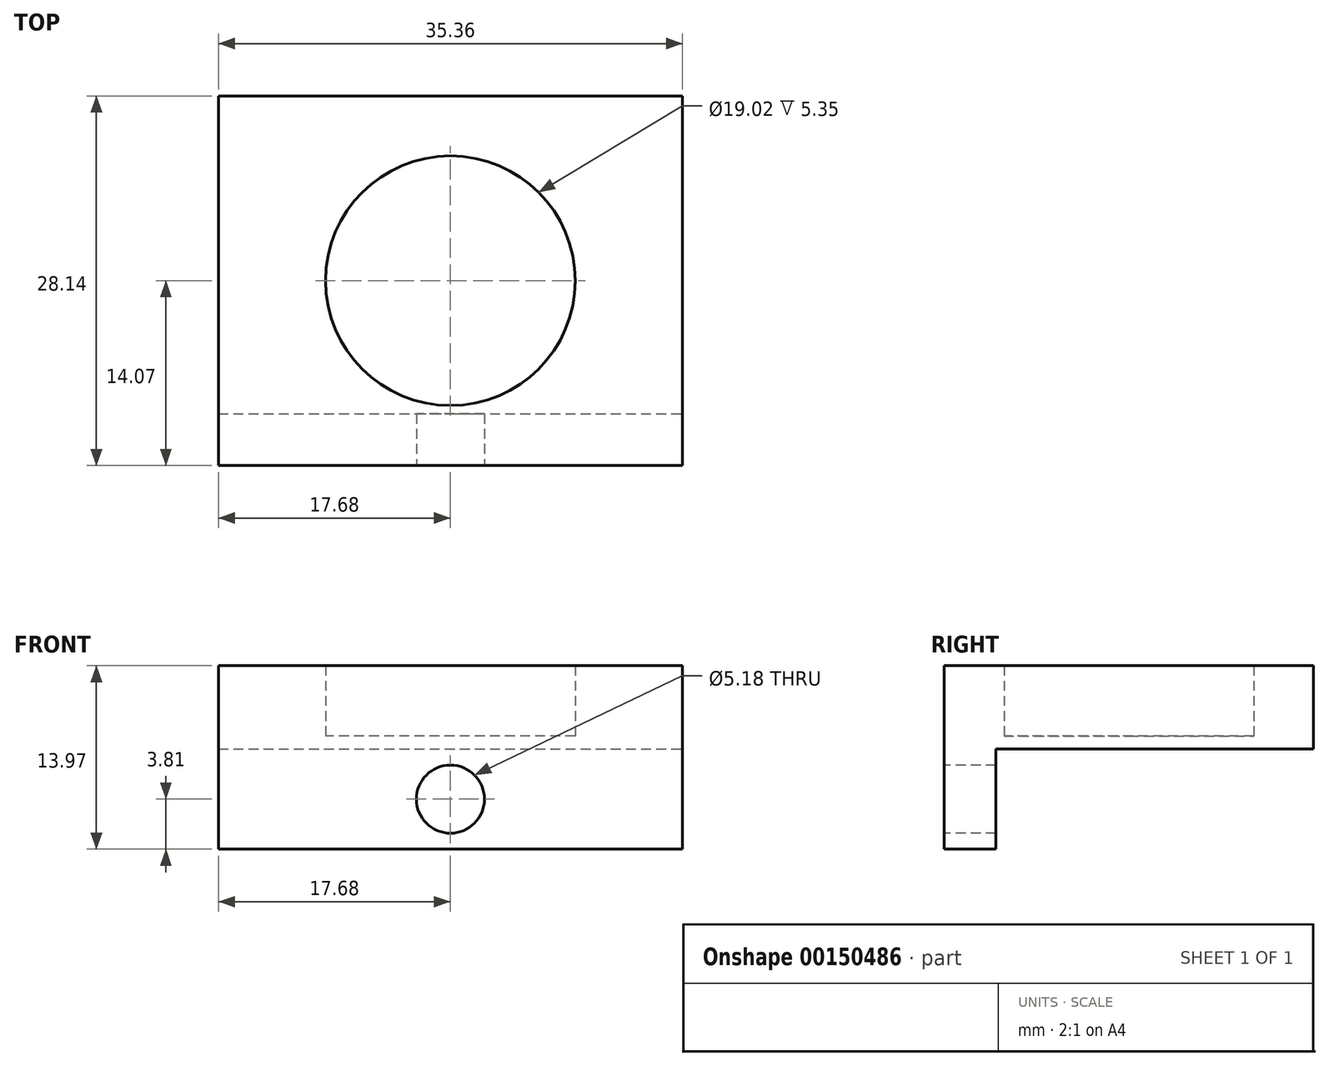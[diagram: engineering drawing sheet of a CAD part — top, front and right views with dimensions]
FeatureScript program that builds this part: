
annotation { "Feature Type Name" : "Feature", "Feature Type Description" : "" }
export const myFeature = defineFeature(function(context is Context, id is Id, definition is map)
    precondition{}
    {
        {
            var Q0;
            Q0=qCreatedBy(makeId("Top.planeOp"),FACE);
            var sketch = newSketch(context, id + "F0", { "sketchPlane" : qUnion([Q0])});
            skLineSegment(sketch, "E0.bottom", {"start": v(-17.68, 14.07) * mm, "end": v(17.68, 14.07) * mm});
            skLineSegment(sketch, "E0.top", {"start": v(-17.68, -14.07) * mm, "end": v(17.68, -14.07) * mm});
            skLineSegment(sketch, "E0.left", {"start": v(-17.68, 14.07) * mm, "end": v(-17.68, -14.07) * mm});
            skLineSegment(sketch, "E0.right", {"start": v(17.68, 14.07) * mm, "end": v(17.68, -14.07) * mm});
            skPoint(sketch, "E0.middle", {"position": v(0, 0) * mm});
            skCircle(sketch, "E1", {"center": v(0, 0) * mm, "radius": 9.5 * mm});
            skSolve(sketch);
        }
        {
            var Q0;
            Q0=makeQuery(id+"F0.imprint","IMPRINT",FACE,{"disambiguationData":[TD([[makeQuery(id+"F0.imprint","IMPRINT",EDGE,{"derivedFrom":sQuery(id+"F0.wireOp",EDGE,"E0.bottom")}),-1.0]])]});
            var Q1;
            Q1=makeQuery(id+"F0.imprint","IMPRINT",FACE,{"disambiguationData":[TD([[makeQuery(id+"F0.imprint","IMPRINT",EDGE,{"derivedFrom":sQuery(id+"F0.wireOp",EDGE,"E1")}),1.0]])]});
            extrude(context, id + "F1", {"entities" : qUnion([Q0, Q1]), "depth" : 1 * mm});
        }
        {
            var Q0;
            Q0 = qSketchRegion(id + "F0", true);
            extrude(context, id + "F2", {"entities" : qUnion([Q0]), "operationType" : NewBodyOperationType.ADD, "depth" : 6.35 * mm});
        }
        {
            var Q0;
            {var subQ0=sQuery(id+"F0.wireOp",EDGE,"E0.top");Q0=makeQuery(id+"F2.boolean.opBoolean","MERGE",FACE,{"derivedFrom":[makeQuery(id+"F1.opExtrude","SWEPT_FACE",FACE,{"disambiguationData":[OSD([subQ0])]}),makeQuery(id+"F2.opExtrude","SWEPT_FACE",FACE,{"disambiguationData":[OSD([subQ0])]})]});}
            var sketch = newSketch(context, id + "F3", { "sketchPlane" : qUnion([Q0])});
            skLineSegment(sketch, "E2.bottom", {"start": v(-17.68, 0) * mm, "end": v(17.68, 0) * mm});
            skLineSegment(sketch, "E2.top", {"start": v(-17.68, -7.62) * mm, "end": v(17.68, -7.62) * mm});
            skLineSegment(sketch, "E2.left", {"start": v(-17.68, 0) * mm, "end": v(-17.68, -7.62) * mm});
            skLineSegment(sketch, "E2.right", {"start": v(17.68, 0) * mm, "end": v(17.68, -7.62) * mm});
            skCircle(sketch, "E3", {"center": v(0, -3.8) * mm, "radius": 2.6 * mm});
            skPoint(sketch, "E3.centerSnap0", {"position": v(-17.68, -3.8) * mm});
            skPoint(sketch, "E3.centerSnap1", {"position": v(0, 0) * mm});
            skLineSegment(sketch, "E4", {"start": v(-17.68, 3.18) * mm, "end": v(17.68, 3.18) * mm, "construction": true});
            skPoint(sketch, "E5.MirrorP", {"position": v(0, 6.35) * mm});
            skLineSegment(sketch, "E6.MirrorCS", {"start": v(-17.68, 13.97) * mm, "end": v(17.68, 13.97) * mm});
            skCircle(sketch, "E7.MirrorC", {"center": v(0, 10.16) * mm, "radius": 2.6 * mm});
            skPoint(sketch, "E8.MirrorP", {"position": v(-17.68, 10.16) * mm});
            skLineSegment(sketch, "E9.MirrorCS", {"start": v(17.68, 6.35) * mm, "end": v(17.68, 13.97) * mm});
            skLineSegment(sketch, "E10.MirrorCS", {"start": v(-17.68, 6.35) * mm, "end": v(17.68, 6.35) * mm});
            skLineSegment(sketch, "E11.MirrorCS", {"start": v(-17.68, 6.35) * mm, "end": v(-17.68, 13.97) * mm});
            skSolve(sketch);
        }
        {
            var Q0;
            Q0=makeQuery(id+"F3.imprint","IMPRINT",FACE,{"disambiguationData":[TD([[makeQuery(id+"F3.imprint","IMPRINT",EDGE,{"derivedFrom":sQuery(id+"F3.wireOp",EDGE,"E2.bottom")}),-1.0]])]});
            extrude(context, id + "F4", {"entities" : qUnion([Q0]), "operationType" : NewBodyOperationType.ADD, "oppositeDirection" : true, "depth" : 3.94 * mm});
        }
    });
